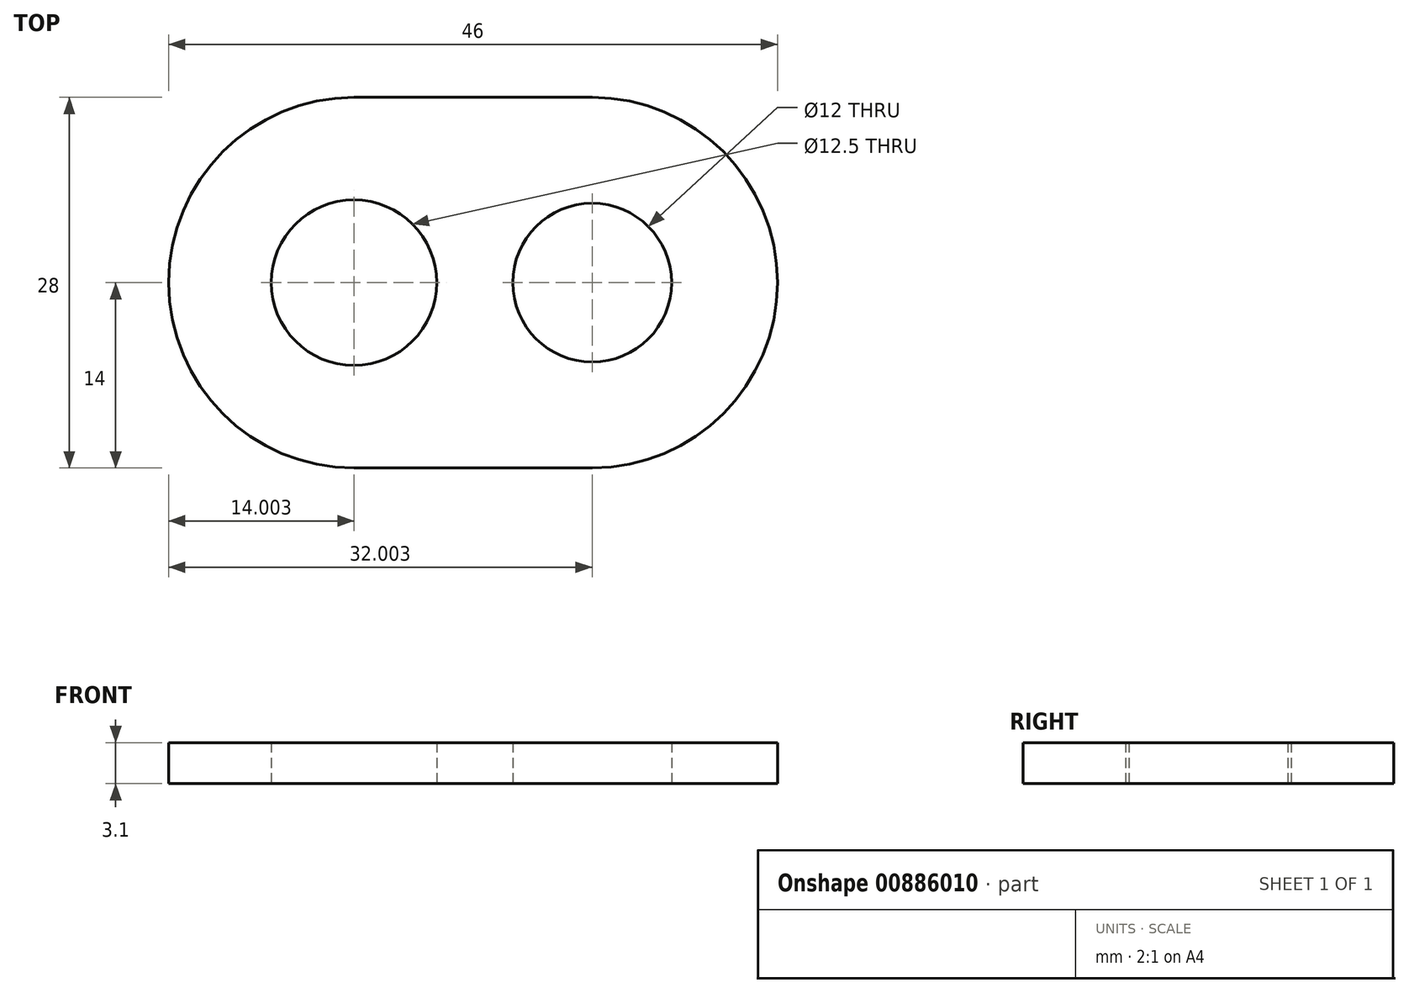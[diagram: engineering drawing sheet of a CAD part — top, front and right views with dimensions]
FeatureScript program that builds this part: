
annotation { "Feature Type Name" : "Feature", "Feature Type Description" : "" }
export const myFeature = defineFeature(function(context is Context, id is Id, definition is map)
    precondition{}
    {
        {
            var Q0;
            Q0=qCreatedBy(makeId("Top.planeOp"),FACE);
            var sketch = newSketch(context, id + "F0", { "sketchPlane" : qUnion([Q0])});
            skCircle(sketch, "E0", {"center": v(0, 0) * mm, "radius": 169 * mm, "construction": true});
            skCircle(sketch, "E1", {"center": v(-34.34, 61) * mm, "radius": 6 * mm});
            skLineSegment(sketch, "E2", {"start": v(-169, 0) * mm, "end": v(-122, 0) * mm});
            skLineSegment(sketch, "E3", {"start": v(-70, 0) * mm, "end": v(-122, 0) * mm});
            skCircle(sketch, "E4", {"center": v(-52.34, 61) * mm, "radius": 6.25 * mm});
            skLineSegment(sketch, "E5", {"start": v(-34.34, 61) * mm, "end": v(-52.34, 61) * mm});
            skCircle(sketch, "E6", {"center": v(-34.34, 61) * mm, "radius": 14 * mm});
            skCircle(sketch, "E7", {"center": v(-52.34, 61) * mm, "radius": 14 * mm});
            skLineSegment(sketch, "E8", {"start": v(-52.34, 75) * mm, "end": v(-34.34, 75) * mm});
            skLineSegment(sketch, "E9", {"start": v(-52.34, 47) * mm, "end": v(-34.34, 47) * mm});
            skSolve(sketch);
        }
        {
            var Q0;
            Q0=qSketchRegion(id+"F0",true);
            var Q1;
            {var subQ5=sQuery(id+"F0.wireOp",EDGE,"E5");var subQ6=sQuery(id+"F0.wireOp",EDGE,"E1");var subQ7=makeQuery(id+"F0.imprint","INTERSECT",VERTEX,{"derivedFrom":[subQ6,subQ5]});Q1=makeQuery(id+"F0.imprint","IMPRINT",FACE,{"disambiguationData":[TD([[makeQuery(id+"F0.imprint","IMPRINT",EDGE,{"disambiguationData":[TD([[subQ7,1.0]])],"derivedFrom":subQ6}),-1.0]])]});}
            var Q2;
            {var subQ5=sQuery(id+"F0.wireOp",EDGE,"E5");var subQ6=sQuery(id+"F0.wireOp",EDGE,"E1");var subQ7=makeQuery(id+"F0.imprint","INTERSECT",VERTEX,{"derivedFrom":[subQ6,subQ5]});Q2=makeQuery(id+"F0.imprint","IMPRINT",FACE,{"disambiguationData":[TD([[makeQuery(id+"F0.imprint","IMPRINT",EDGE,{"disambiguationData":[TD([[subQ7,-1.0]])],"derivedFrom":subQ6}),-1.0]])]});}
            var Q3;
            {var subQ0=sQuery(id+"F0.wireOp",EDGE,"E7");var subQ1=sQuery(id+"F0.wireOp",EDGE,"E1");var subQ2=makeQuery(id+"F0.imprint","INTERSECT",VERTEX,{"disambiguationData":[OD(1.0)],"derivedFrom":[subQ1,subQ0]});Q3=makeQuery(id+"F0.imprint","IMPRINT",FACE,{"disambiguationData":[TD([[makeQuery(id+"F0.imprint","IMPRINT",EDGE,{"disambiguationData":[TD([[subQ2,-1.0]])],"derivedFrom":subQ1}),-1.0]])]});}
            var Q4;
            {var subQ0=sQuery(id+"F0.wireOp",EDGE,"9kZ8H6KI-7roA-TIT5-uAgb-u4CkBlDGA7dT");var subQ1=sQuery(id+"F0.wireOp",EDGE,"5bNudcUO-3Cp7-s35Z-9Ye9-rIpnnfFkjyt3");var subQ2=makeQuery(id+"F0.imprint","INTERSECT",VERTEX,{"disambiguationData":[OD(0.0)],"derivedFrom":[subQ1,subQ0]});Q4=makeQuery(id+"F0.imprint","IMPRINT",FACE,{"disambiguationData":[TD([[makeQuery(id+"F0.imprint","IMPRINT",EDGE,{"disambiguationData":[TD([[subQ2,1.0]])],"derivedFrom":subQ1}),-1.0]])]});}
            var Q5;
            {var subQ3=sQuery(id+"F0.wireOp",EDGE,"9kZ8H6KI-7roA-TIT5-uAgb-u4CkBlDGA7dT");var subQ6=sQuery(id+"F0.wireOp",EDGE,"5bNudcUO-3Cp7-s35Z-9Ye9-rIpnnfFkjyt3");var subQ9=makeQuery(id+"F0.imprint","INTERSECT",VERTEX,{"disambiguationData":[OD(0.0)],"derivedFrom":[subQ6,subQ3]});Q5=makeQuery(id+"F0.imprint","IMPRINT",FACE,{"disambiguationData":[TD([[makeQuery(id+"F0.imprint","IMPRINT",EDGE,{"disambiguationData":[TD([[subQ9,-1.0]])],"derivedFrom":subQ6}),-1.0]])]});}
            var Q6;
            {var subQ5=sQuery(id+"F0.wireOp",EDGE,"S0uz2u0M-lSkC-bxsg-xzQw-cyeuq6uNyWC9");var subQ7=sQuery(id+"F0.wireOp",EDGE,"5bNudcUO-3Cp7-s35Z-9Ye9-rIpnnfFkjyt3");var subQ8=makeQuery(id+"F0.imprint","INTERSECT",VERTEX,{"derivedFrom":[subQ7,subQ5]});Q6=makeQuery(id+"F0.imprint","IMPRINT",FACE,{"disambiguationData":[TD([[makeQuery(id+"F0.imprint","IMPRINT",EDGE,{"disambiguationData":[TD([[subQ8,-1.0]])],"derivedFrom":subQ7}),-1.0]])]});}
            extrude(context, id + "F1", {"entities" : qUnion([Q0, Q1, Q2, Q3, Q4, Q5, Q6]), "depth" : 3.1 * mm, "offsetDistance" : 25 * mm});
        }
        {
            var Q0;
            Q0 = qSketchRegion(id + "F0", true);
            extrude(context, id + "F2", {"entities" : qUnion([Q0]), "operationType" : NewBodyOperationType.ADD, "depth" : 3.1 * mm, "offsetDistance" : 25 * mm});
        }
    });
